# Revit family: НЕВАТОМ_Фильтр-бокс AxB FVK, Версия 2
name_source: partatom
category: Арматура воздуховодов
revit_build: Autodesk Revit 2017 (Build: 20170118_1100(x64)
units: mm (PartAtom-declared; Revit-internal decimal feet)

## family parameters
Всегда вертикально = Нет
На основе рабочей плоскости = Нет
Общий = Нет
При загрузке вырезать с полостями = Нет
Размер круглого соединителя = Использовать диаметр
Тип детали = Вставляется

## types (11) — shared parameters
ADSK_Единица измерения = шт.
ADSK_Завод-изготовитель = НЕВАТОМ
ADSK_Количество = 1
ADSK_Масса_Текст = кг
ADSK_Материал наименование = Оцинкованная сталь
ADSK_Наименование = Фильтр-бокс FVK
Nevatom_URL = https://t.me
t = 2 мм
Материал корпуса = Оцинкованная сталь
НЕВАТОМ_Сменная касета = FVK
Фланец = 30 мм

## per-type parameters (varying)
| type | ADSK_Марка |
| ФИЛЬТР-БОКС FVK –300x150–ОЦ. | FVK –300x150–ОЦ. |
| ФИЛЬТР-БОКС FVK–400x200–ОЦ. | FVK–400x200–ОЦ. |
| ФИЛЬТР-БОКС FVK– 500x250–ОЦ. | FVK– 500x250–ОЦ. |
| ФИЛЬТР-БОКС FVK –500x300–ОЦ. | FVK –500x300–ОЦ |
| ФИЛЬТР-БОКС FVK –600x300–ОЦ. | FVK –600x300–ОЦ. |
| ФИЛЬТР-БОКС FVK –600x350–ОЦ. | FVK –600x350–ОЦ. |
| ФИЛЬТР-БОКС FVK– 700x400–ОЦ. | FVK– 700x400–ОЦ. |
| ФИЛЬТР-БОКС FVK– 800x500–ОЦ. | FVK– 800x500–ОЦ. |
| ФИЛЬТР-БОКС FVK– 900x500–ОЦ. | FVK– 900x500–ОЦ. |
| ФИЛЬТР-БОКС FVK– 1000x500–ОЦ. | FVK– 1000x500–ОЦ. |
| ФИЛЬТР-БОКС FVK– 1000x1000–ОЦ. | FVK– 1000x1000–ОЦ |
